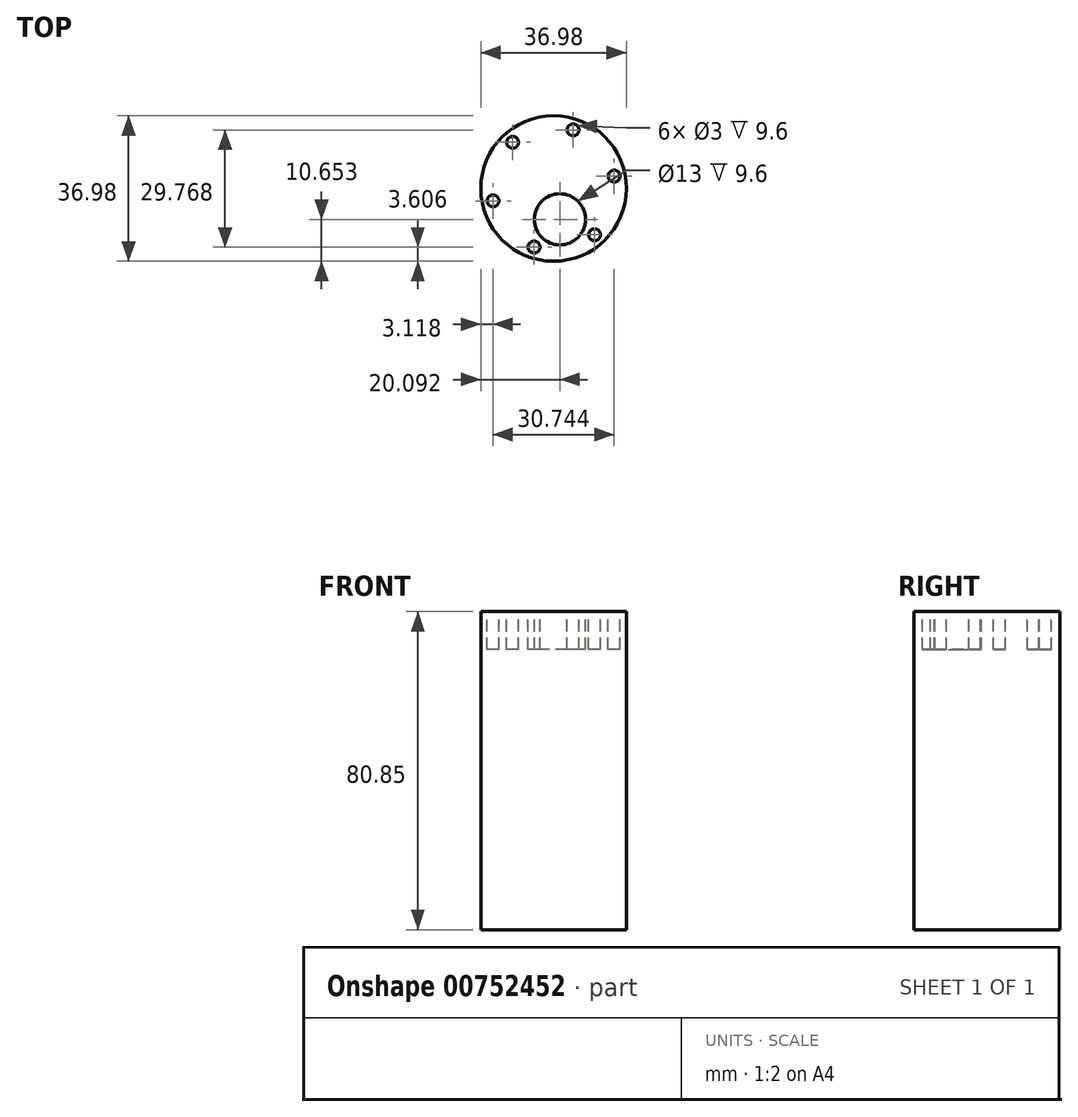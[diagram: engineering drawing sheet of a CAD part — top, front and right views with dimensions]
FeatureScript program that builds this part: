
annotation { "Feature Type Name" : "Feature", "Feature Type Description" : "" }
export const myFeature = defineFeature(function(context is Context, id is Id, definition is map)
    precondition{}
    {
        {
            var Q0;
            Q0=qCreatedBy(makeId("Top.planeOp"),FACE);
            var sketch = newSketch(context, id + "F0", { "sketchPlane" : qUnion([Q0])});
            skCircle(sketch, "E0", {"center": v(0, 0) * mm, "radius": 18.49 * mm});
            skSolve(sketch);
        }
        {
            var Q0;
            Q0 = qSketchRegion(id + "F0", true);
            extrude(context, id + "F1", {"entities" : qUnion([Q0]), "depth" : 80.85 * mm, "offsetDistance" : 25.4 * mm});
        }
        {
            var Q0;
            Q0=makeQuery(id+"F1.opExtrude","CAP_FACE",FACE,{"disambiguationData":[OSD([sQuery(id+"F0.wireOp",EDGE,"E0")])],"isStart":false});
            var sketch = newSketch(context, id + "F2", { "sketchPlane" : qUnion([Q0])});
            skCircle(sketch, "E1", {"center": v(10.4, -11.74) * mm, "radius": 1.5 * mm});
            skLineSegment(sketch, "E2", {"start": v(10.4, -11.74) * mm, "end": v(0, 0) * mm, "construction": true});
            skPoint(sketch, "E3.center", {"position": v(0, 0) * mm});
            skCircle(sketch, "E4.1.0", {"center": v(15.37, 3.14) * mm, "radius": 1.5 * mm});
            skCircle(sketch, "E4.2.0", {"center": v(4.96, 14.88) * mm, "radius": 1.5 * mm});
            skCircle(sketch, "E4.3.0", {"center": v(-10.4, 11.74) * mm, "radius": 1.5 * mm});
            skCircle(sketch, "E4.4.0", {"center": v(-15.37, -3.14) * mm, "radius": 1.5 * mm});
            skCircle(sketch, "E4.5.0", {"center": v(-4.96, -14.88) * mm, "radius": 1.5 * mm});
            skCircle(sketch, "E5", {"center": v(1.6, -7.84) * mm, "radius": 6.5 * mm});
            skLineSegment(sketch, "E6", {"start": v(-4.96, -14.88) * mm, "end": v(10.4, -11.74) * mm, "construction": true});
            skLineSegment(sketch, "E7", {"start": v(2.72, -13.31) * mm, "end": v(-1.4, 6.89) * mm, "construction": true});
            skSolve(sketch);
        }
        {
            var Q0;
            Q0 = qSketchRegion(id + "F2", true);
            extrude(context, id + "F3", {"entities" : qUnion([Q0]), "operationType" : NewBodyOperationType.REMOVE, "oppositeDirection" : true, "depth" : 9.6 * mm, "offsetDistance" : 25.4 * mm});
        }
    });
